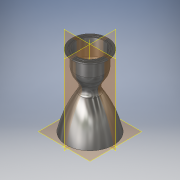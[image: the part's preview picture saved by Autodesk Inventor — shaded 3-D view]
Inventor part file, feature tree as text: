
AUTODESK INVENTOR PART (.ipt)
format: ipt  version: 2017 (Build 210142000, 142)  size: 275,968 bytes
history: native  units: in
note: dims shown in document units (in); Inventor stores cm internally (conversion verified against a paired STEP export)
features: move_body x5, fillet x4, other x2
ambient origin geometry x8: Origin, YZ Plane, XZ Plane, XY Plane, X Axis, Y Axis, Z Axis, Center Point
bodies: Body1 (feature_tree)
feature tree (11):
  other  "CD Nozzle"
  fillet  "Fillet14"  [1 undecoded]
  fillet  "Fillet15"  Radius=1.7717in
  fillet  "Fillet16"  Radius=1.378in
  fillet  "Fillet17"  Radius=0.5906in
  move_body  "Move Body1"
  move_body  "Move Body2"
  move_body  "Move Body3"
  move_body  "Move Body4"
  move_body  "Move Body5"
  other  "CD Nozzle Sketch"
note: 1 required parameter value undecoded (feature->parameter linkage not recoverable at this tier; creation-order binding heuristic only, values carry confidence <= 0.55)
